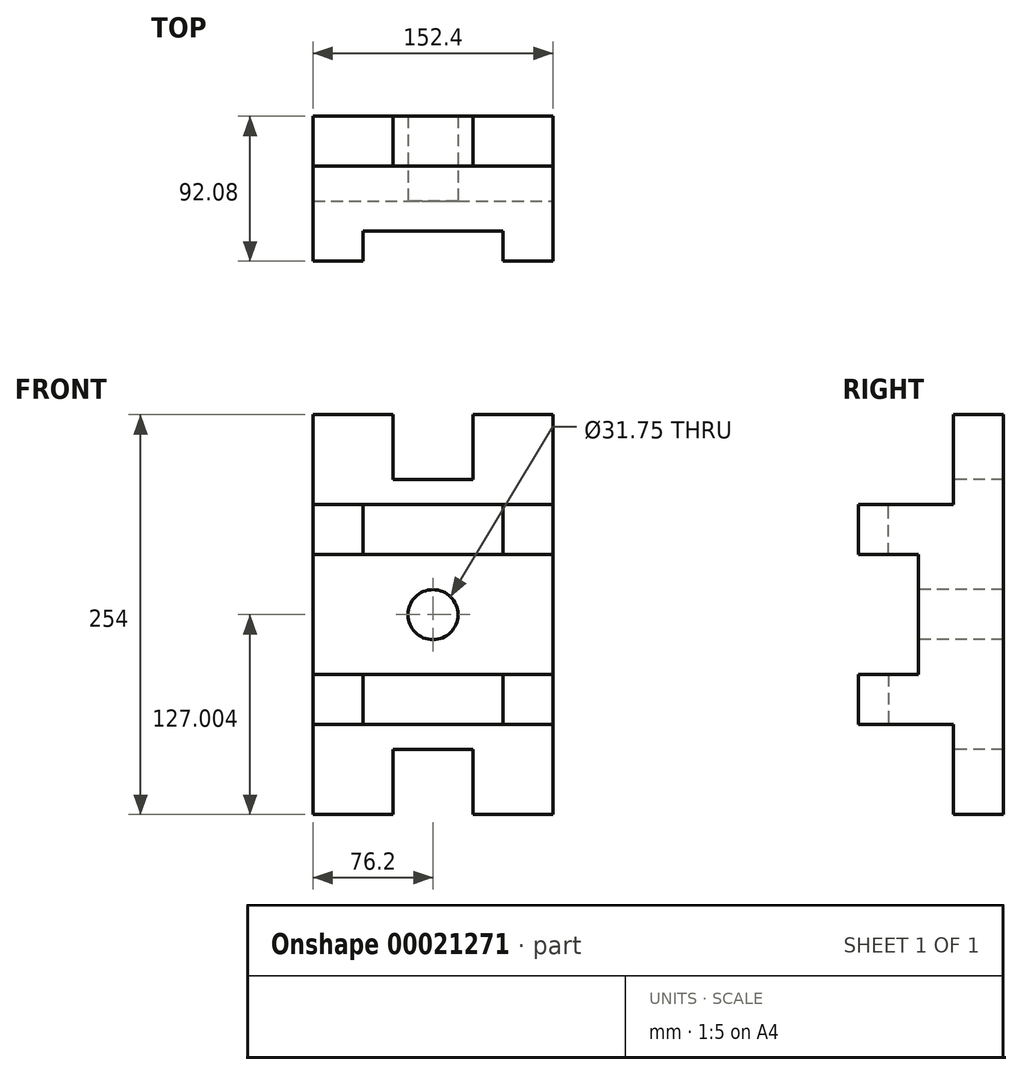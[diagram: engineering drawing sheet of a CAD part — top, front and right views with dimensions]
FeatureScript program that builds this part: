
annotation { "Feature Type Name" : "Feature", "Feature Type Description" : "" }
export const myFeature = defineFeature(function(context is Context, id is Id, definition is map)
    precondition{}
    {
        {
            var Q0;
            Q0=qCreatedBy(makeId("Front.planeOp"),FACE);
            var sketch = newSketch(context, id + "F0", { "sketchPlane" : qUnion([Q0])});
            skLineSegment(sketch, "E0.bottom", {"start": v(-76.2, 75.87) * mm, "end": v(76.2, 75.87) * mm});
            skLineSegment(sketch, "E0.top", {"start": v(-76.2, -51.13) * mm, "end": v(76.2, -51.13) * mm});
            skLineSegment(sketch, "E0.left", {"start": v(-76.2, 75.87) * mm, "end": v(-76.2, -51.13) * mm});
            skLineSegment(sketch, "E0.right", {"start": v(76.2, 75.87) * mm, "end": v(76.2, -51.13) * mm});
            skSolve(sketch);
        }
        {
            var Q0;
            Q0=makeQuery(id+"F0.imprint","IMPRINT",FACE,{"disambiguationData":[TD([[makeQuery(id+"F0.imprint","IMPRINT",EDGE,{"derivedFrom":sQuery(id+"F0.wireOp",EDGE,"E0.bottom")}),-1.0]])]});
            extrude(context, id + "F1", {"entities" : qUnion([Q0]), "depth" : 92.07 * mm});
        }
        {
            var Q0;
            Q0=makeQuery(id+"F1.opExtrude","CAP_FACE",FACE,{"disambiguationData":[OSD([sQuery(id+"F0.wireOp",EDGE,"E0.bottom"),sQuery(id+"F0.wireOp",EDGE,"E0.top"),sQuery(id+"F0.wireOp",EDGE,"E0.left"),sQuery(id+"F0.wireOp",EDGE,"E0.right")])],"isStart":false});
            var sketch = newSketch(context, id + "F2", { "sketchPlane" : qUnion([Q0])});
            skLineSegment(sketch, "E1.top", {"start": v(-25.4, -9.85) * mm, "end": v(25.4, -9.85) * mm});
            skLineSegment(sketch, "E1.left", {"start": v(-25.4, -51.13) * mm, "end": v(-25.4, -9.85) * mm});
            skLineSegment(sketch, "E1.right", {"start": v(25.4, -51.13) * mm, "end": v(25.4, -9.85) * mm});
            skCircle(sketch, "E2", {"center": v(0, 75.87) * mm, "radius": 15.88 * mm});
            skLineSegment(sketch, "E3.bottom", {"start": v(-76.2, 37.77) * mm, "end": v(76.2, 37.77) * mm});
            skLineSegment(sketch, "E3.top", {"start": v(-76.2, 6.02) * mm, "end": v(76.2, 6.02) * mm});
            skLineSegment(sketch, "E3.left", {"start": v(-76.2, 37.77) * mm, "end": v(-76.2, 6.02) * mm});
            skLineSegment(sketch, "E3.right", {"start": v(76.2, 37.77) * mm, "end": v(76.2, 6.02) * mm});
            skLineSegment(sketch, "E4", {"start": v(-44.45, 37.77) * mm, "end": v(-44.45, 6.02) * mm});
            skLineSegment(sketch, "E5", {"start": v(44.45, 37.77) * mm, "end": v(44.45, 6.02) * mm});
            skSolve(sketch);
        }
        {
            var Q0;
            {var subQ3=makeQuery(id+"F1.opExtrude","CAP_EDGE",EDGE,{"disambiguationData":[OSD([sQuery(id+"F0.wireOp",EDGE,"E0.bottom")])],"isStart":false});var subQ5=sQuery(id+"F2.wireOp",EDGE,"E2");var subQ9=makeQuery(id+"F2.imprint","INTERSECT",VERTEX,{"disambiguationData":[OD(0.0)],"derivedFrom":[subQ3,subQ5]});Q0=makeQuery(id+"F2.imprint","IMPRINT",FACE,{"disambiguationData":[TD([[makeQuery(id+"F2.imprint","IMPRINT",EDGE,{"disambiguationData":[TD([[subQ9,-1.0]])],"derivedFrom":subQ5}),-1.0]])]});}
            var sketch = newSketch(context, id + "F3", { "sketchPlane" : qUnion([Q0])});
            skSolve(sketch);
        }
        {
            var Q0;
            {var subQ0=sQuery(id+"F2.wireOp",EDGE,"E4");Q0=makeQuery(id+"F2.imprint","IMPRINT",FACE,{"disambiguationData":[TD([[makeQuery(id+"F2.imprint","IMPRINT",EDGE,{"derivedFrom":subQ0}),1.0]])]});}
            extrude(context, id + "F4", {"entities" : qUnion([Q0]), "operationType" : NewBodyOperationType.REMOVE, "oppositeDirection" : true, "depth" : 19.05 * mm});
        }
        {
            var Q0;
            {var subQ3=makeQuery(id+"F1.opExtrude","CAP_EDGE",EDGE,{"disambiguationData":[OSD([sQuery(id+"F0.wireOp",EDGE,"E0.bottom")])],"isStart":false});var subQ8=sQuery(id+"F2.wireOp",EDGE,"E2");var subQ10=makeQuery(id+"F2.imprint","INTERSECT",VERTEX,{"disambiguationData":[OD(0.0)],"derivedFrom":[subQ3,subQ8]});Q0=makeQuery(id+"F3.imprint","IMPRINT",FACE,{"disambiguationData":[TD([[makeQuery(id+"F3.imprint","IMPRINT",EDGE,{"derivedFrom":makeQuery(id+"F2.imprint","IMPRINT",EDGE,{"disambiguationData":[TD([[subQ10,-1.0]])],"derivedFrom":subQ8})}),-1.0]])]});}
            extrude(context, id + "F5", {"entities" : qUnion([Q0]), "operationType" : NewBodyOperationType.REMOVE, "oppositeDirection" : true, "depth" : 38.1 * mm});
        }
        {
            var Q0;
            {var subQ0=sQuery(id+"F0.wireOp",EDGE,"E0.bottom");Q0=makeQuery(id+"F5.boolean.opBoolean","SPLIT",FACE,{"disambiguationData":[TD([makeQuery(id+"F1.opExtrude","SWEPT_FACE",FACE,{"disambiguationData":[OSD([subQ0])]})])],"derivedFrom":makeQuery(id+"F1.opExtrude","CAP_FACE",FACE,{"disambiguationData":[OSD([subQ0,sQuery(id+"F0.wireOp",EDGE,"E0.top"),sQuery(id+"F0.wireOp",EDGE,"E0.left"),sQuery(id+"F0.wireOp",EDGE,"E0.right")])],"isStart":false})});}
            extrude(context, id + "F6", {"entities" : qUnion([Q0]), "operationType" : NewBodyOperationType.REMOVE, "oppositeDirection" : true, "depth" : 38.1 * mm});
        }
        {
            var Q0;
            Q0=makeQuery(id+"F2.imprint","IMPRINT",FACE,{"disambiguationData":[TD([[makeQuery(id+"F2.imprint","IMPRINT",EDGE,{"derivedFrom":sQuery(id+"F2.wireOp",EDGE,"E1.top")}),1.0]])]});
            extrude(context, id + "F7", {"entities" : qUnion([Q0]), "operationType" : NewBodyOperationType.REMOVE, "oppositeDirection" : true, "depth" : 60.32 * mm});
        }
        {
            var Q0;
            Q0=makeQuery(id+"F2.imprint","IMPRINT",FACE,{"disambiguationData":[TD([[makeQuery(id+"F2.imprint","IMPRINT",EDGE,{"derivedFrom":sQuery(id+"F2.wireOp",EDGE,"E1.top")}),-1.0]])]});
            extrude(context, id + "F8", {"entities" : qUnion([Q0]), "operationType" : NewBodyOperationType.REMOVE, "oppositeDirection" : true, "depth" : 92.07 * mm});
        }
        {
            var Q0;
            {var subQ0=sQuery(id+"F0.wireOp",EDGE,"E0.bottom");var subQ1=sQuery(id+"F0.wireOp",EDGE,"E0.left");var subQ2=sQuery(id+"F0.wireOp",EDGE,"E0.right");Q0=makeQuery(id+"F6.boolean.opBoolean","MERGE",FACE,{"derivedFrom":[makeQuery(id+"F5.boolean.opBoolean","COPY",FACE,{"derivedFrom":makeQuery(id+"F5.opExtrude","CAP_FACE",FACE,{"disambiguationData":[OSD([subQ0,subQ1,subQ2,sQuery(id+"F2.wireOp",EDGE,"E2"),sQuery(id+"F2.wireOp",EDGE,"E3.bottom")])],"isStart":false})}),makeQuery(id+"F6.opExtrude","CAP_FACE",FACE,{"disambiguationData":[OSD([subQ0,sQuery(id+"F0.wireOp",EDGE,"E0.top"),subQ1,subQ2])],"isStart":false})]});}
            var sketch = newSketch(context, id + "F9", { "sketchPlane" : qUnion([Q0])});
            skCircle(sketch, "E6", {"center": v(0, 75.87) * mm, "radius": 15.88 * mm});
            skSolve(sketch);
        }
        {
            var Q0;
            Q0 = qSketchRegion(id + "F9", true);
            extrude(context, id + "F10", {"entities" : qUnion([Q0]), "operationType" : NewBodyOperationType.REMOVE, "oppositeDirection" : true, "depth" : 53.97 * mm});
        }
        {
            var Q0;
            Q0=makeQuery(id+"F1.opExtrude","SWEPT_BODY",BODY,{"disambiguationData":[OSD([sQuery(id+"F0.wireOp",EDGE,"E0.bottom"),sQuery(id+"F0.wireOp",EDGE,"E0.top"),sQuery(id+"F0.wireOp",EDGE,"E0.left"),sQuery(id+"F0.wireOp",EDGE,"E0.right")])]});
            var Q1;
            {var subQ0=sQuery(id+"F0.wireOp",EDGE,"E0.bottom");var subQ3=sQuery(id+"F0.wireOp",EDGE,"E0.right");Q1=makeQuery(id+"F10.boolean.opBoolean","SPLIT",FACE,{"disambiguationData":[TD([makeQuery(id+"F1.opExtrude","SWEPT_FACE",FACE,{"disambiguationData":[OSD([subQ3])]})])],"derivedFrom":makeQuery(id+"F1.opExtrude","SWEPT_FACE",FACE,{"disambiguationData":[OSD([subQ0])]})});}
            mirror(context, id + "F11", {"operationType" : NewBodyOperationType.ADD, "entities" : qUnion([Q0]), "mirrorPlane" : qUnion([Q1])});
        }
    });
